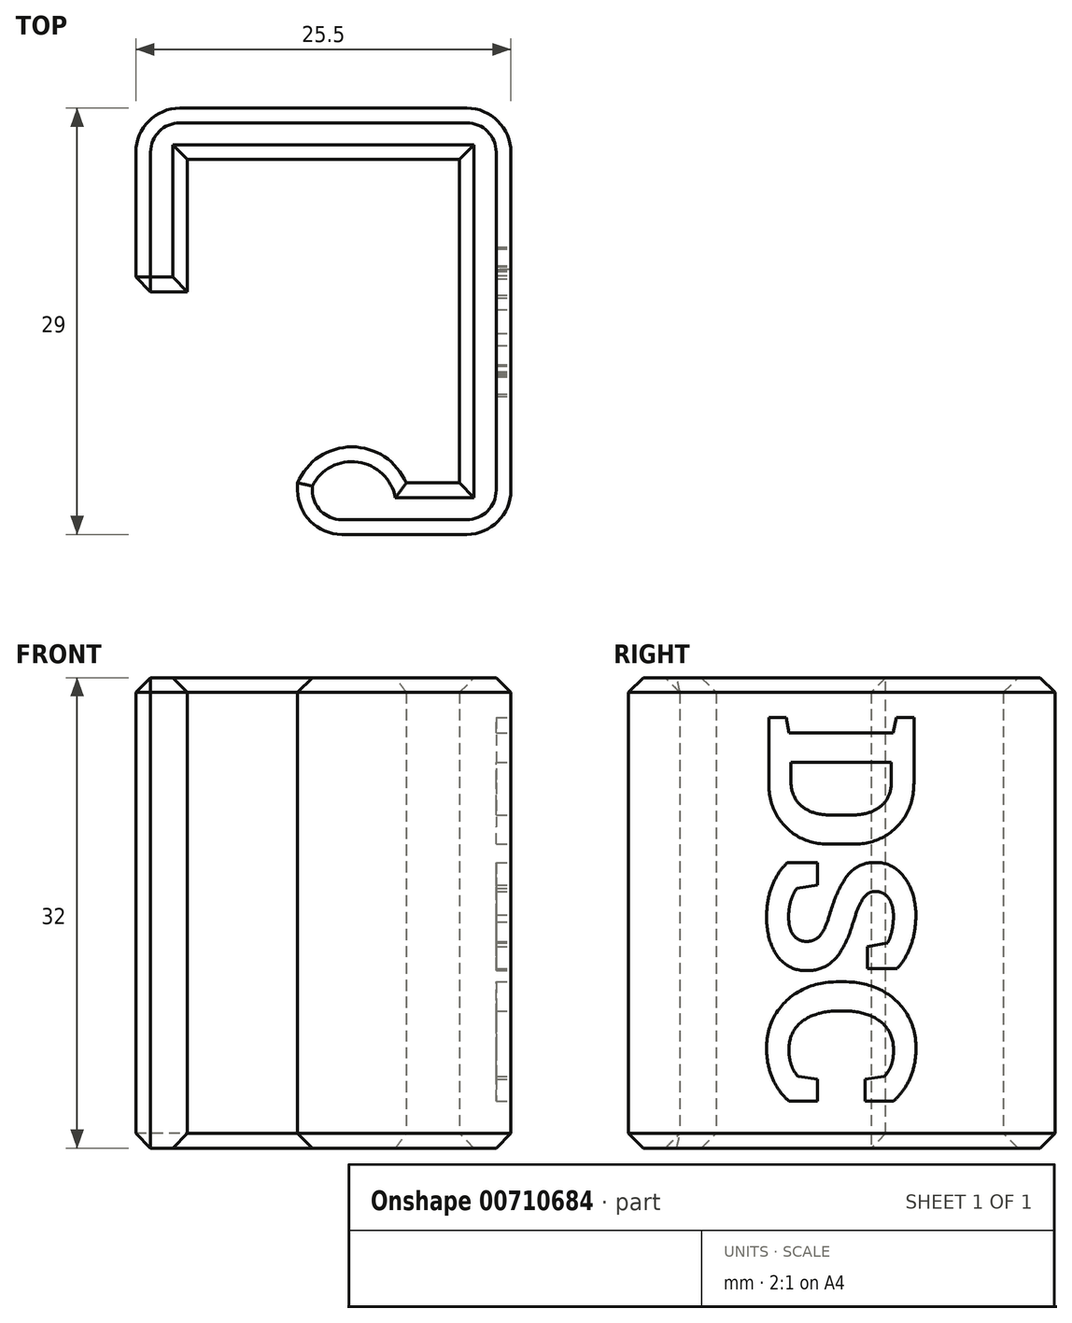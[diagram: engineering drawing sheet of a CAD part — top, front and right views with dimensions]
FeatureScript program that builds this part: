
annotation { "Feature Type Name" : "Feature", "Feature Type Description" : "" }
export const myFeature = defineFeature(function(context is Context, id is Id, definition is map)
    precondition{}
    {
        {
            var Q0;
            Q0=qCreatedBy(makeId("Top.planeOp"),FACE);
            var sketch = newSketch(context, id + "F0", { "sketchPlane" : qUnion([Q0])});
            skLineSegment(sketch, "E0", {"start": v(-14.4, 16.46) * mm, "end": v(-14.4, 25.46) * mm});
            skLineSegment(sketch, "E1", {"start": v(-14.4, 25.46) * mm, "end": v(4.1, 25.46) * mm});
            skLineSegment(sketch, "E2", {"start": v(4.1, 25.46) * mm, "end": v(4.1, 3.46) * mm});
            skLineSegment(sketch, "E3", {"start": v(4.1, 3.46) * mm, "end": v(0.48, 3.46) * mm});
            skArc(sketch, "E4", {"start": v(0.48, 3.46) * mm, "mid": v(-3.21, 5.91) * mm, "end": v(-6.9, 3.46) * mm});
            skLineSegment(sketch, "E5", {"start": v(-14.4, 16.46) * mm, "end": v(-17.9, 16.46) * mm});
            skLineSegment(sketch, "E6", {"start": v(-17.9, 16.46) * mm, "end": v(-17.9, 25.96) * mm});
            skLineSegment(sketch, "E7", {"start": v(-14.9, 28.96) * mm, "end": v(4.6, 28.96) * mm});
            skLineSegment(sketch, "E8", {"start": v(7.6, 25.96) * mm, "end": v(7.6, 2.96) * mm});
            skLineSegment(sketch, "E9", {"start": v(4.6, -0.04) * mm, "end": v(-3.9, -0.04) * mm});
            skLineSegment(sketch, "E10", {"start": v(-6.9, 2.96) * mm, "end": v(-6.9, 3.46) * mm});
            skPoint(sketch, "E11.visualSharp", {"position": v(-17.9, 28.96) * mm});
            skArc(sketch, "E11.filletArc", {"start": v(-14.9, 28.96) * mm, "mid": v(-17.02, 28.08) * mm, "end": v(-17.9, 25.96) * mm});
            skPoint(sketch, "E12.visualSharp", {"position": v(7.6, 28.96) * mm});
            skArc(sketch, "E12.filletArc", {"start": v(7.6, 25.96) * mm, "mid": v(6.72, 28.08) * mm, "end": v(4.6, 28.96) * mm});
            skPoint(sketch, "E13.visualSharp", {"position": v(7.6, -0.04) * mm});
            skArc(sketch, "E13.filletArc", {"start": v(4.6, -0.04) * mm, "mid": v(6.72, 0.84) * mm, "end": v(7.6, 2.96) * mm});
            skPoint(sketch, "E14.visualSharp", {"position": v(-6.9, -0.04) * mm});
            skArc(sketch, "E14.filletArc", {"start": v(-6.9, 2.96) * mm, "mid": v(-6.02, 0.84) * mm, "end": v(-3.9, -0.04) * mm});
            skSolve(sketch);
        }
        {
            var Q0;
            Q0=makeQuery(id+"F0.imprint","IMPRINT",FACE,{"disambiguationData":[TD([[makeQuery(id+"F0.imprint","IMPRINT",EDGE,{"derivedFrom":sQuery(id+"F0.wireOp",EDGE,"E0")}),1.0]])]});
            extrude(context, id + "F1", {"entities" : qUnion([Q0]), "depth" : 32 * mm, "offsetDistance" : 25 * mm});
        }
        {
            var Q0;
            Q0=makeQuery(id+"F1.opExtrude","CAP_EDGE",EDGE,{"disambiguationData":[OSD([sQuery(id+"F0.wireOp",EDGE,"E1")])],"isStart":false});
            var Q1;
            Q1=makeQuery(id+"F1.opExtrude","CAP_EDGE",EDGE,{"disambiguationData":[OSD([sQuery(id+"F0.wireOp",EDGE,"E2")])],"isStart":false});
            var Q2;
            Q2=makeQuery(id+"F1.opExtrude","CAP_EDGE",EDGE,{"disambiguationData":[OSD([sQuery(id+"F0.wireOp",EDGE,"E3")])],"isStart":false});
            var Q3;
            Q3=makeQuery(id+"F1.opExtrude","CAP_EDGE",EDGE,{"disambiguationData":[OSD([sQuery(id+"F0.wireOp",EDGE,"E4")])],"isStart":false});
            var Q4;
            Q4=makeQuery(id+"F1.opExtrude","CAP_EDGE",EDGE,{"disambiguationData":[OSD([sQuery(id+"F0.wireOp",EDGE,"E9")])],"isStart":false});
            var Q5;
            Q5=makeQuery(id+"F1.opExtrude","CAP_EDGE",EDGE,{"disambiguationData":[OSD([sQuery(id+"F0.wireOp",EDGE,"E5")])],"isStart":false});
            var Q6;
            Q6=makeQuery(id+"F1.opExtrude","CAP_EDGE",EDGE,{"disambiguationData":[OSD([sQuery(id+"F0.wireOp",EDGE,"E0")])],"isStart":false});
            var Q7;
            Q7=makeQuery(id+"F1.opExtrude","SWEPT_EDGE",EDGE,{"disambiguationData":[OSD([sQuery(id+"F0.wireOp",EDGE,"E5"),sQuery(id+"F0.wireOp",EDGE,"E6")])]});
            var Q8;
            Q8=makeQuery(id+"F1.opExtrude","CAP_EDGE",EDGE,{"disambiguationData":[OSD([sQuery(id+"F0.wireOp",EDGE,"E6")])],"isStart":true});
            var Q9;
            Q9=makeQuery(id+"F1.opExtrude","CAP_EDGE",EDGE,{"disambiguationData":[OSD([sQuery(id+"F0.wireOp",EDGE,"E0")])],"isStart":true});
            var Q10;
            Q10=makeQuery(id+"F1.opExtrude","CAP_EDGE",EDGE,{"disambiguationData":[OSD([sQuery(id+"F0.wireOp",EDGE,"E1")])],"isStart":true});
            var Q11;
            Q11=makeQuery(id+"F1.opExtrude","CAP_EDGE",EDGE,{"disambiguationData":[OSD([sQuery(id+"F0.wireOp",EDGE,"E2")])],"isStart":true});
            var Q12;
            Q12=makeQuery(id+"F1.opExtrude","CAP_EDGE",EDGE,{"disambiguationData":[OSD([sQuery(id+"F0.wireOp",EDGE,"E3")])],"isStart":true});
            var Q13;
            Q13=makeQuery(id+"F1.opExtrude","CAP_EDGE",EDGE,{"disambiguationData":[OSD([sQuery(id+"F0.wireOp",EDGE,"E4")])],"isStart":true});
            chamfer(context, id + "F2", {"entities" : qUnion([Q0, Q1, Q2, Q3, Q4, Q5, Q6, Q7, Q8, Q9, Q10, Q11, Q12, Q13]), "width" : 1 * mm, "tangentPropagation" : true});
        }
        {
            var Q0;
            Q0=makeQuery(id+"F1.opExtrude","SWEPT_FACE",FACE,{"disambiguationData":[OSD([sQuery(id+"F0.wireOp",EDGE,"E8")])]});
            var sketch = newSketch(context, id + "F3", { "sketchPlane" : qUnion([Q0])});
            skText(sketch, "E15", { "text": "DSC", "fontName": "RobotoSlab-Bold.ttf"});
            const initialGuessF3  = {"E15": [0.0095, 0.02966, 0, -1, 0.01]};
            skSetInitialGuess(sketch, initialGuessF3);
            skSolve(sketch);
        }
        {
            var Q0;
            Q0 = qSketchRegion(id + "F3", true);
            extrude(context, id + "F4", {"entities" : qUnion([Q0]), "operationType" : NewBodyOperationType.REMOVE, "oppositeDirection" : true, "depth" : 1 * mm, "offsetDistance" : 25 * mm});
        }
    });
